# Revit family: Montageschiene 27- 18-1,25 fbv 2m Langloch 2D
name_source: partatom
category: HLS-Bauteile
units: mm (PartAtom-declared; Revit-internal decimal feet)

## family parameters
Arbeitsebenenbasiert = Ja
Beim Laden mit Abzugskörper schneiden = Nein
Bemaßung runder Anschluss = Durchmesser verwenden
Beschriftungsausrichtung beibehalten = Nein
Gemeinsam genutzt = Ja
Immer vertikal = Nein
Raumberechnungspunkt = Nein
Teiletyp = Normal

## types (1)
- Profil  27- 18-1,25 fbv L=2000
    Abmessung = 27/18/1.25 mm
    Artikelnummer = 1240013
    Breite = 27 mm  [stored 0.0885827 ft]
    Bund = 800 m
    EAN = 4250928424259
    Fabrikat = MEFA
    Firma = MEFA Befestigungs- und Montagesysteme GmbH
    Fläche (schwächster Profilquerschnitt) = 0 m²
    Gewicht = 0,60 kg
    Höhe = 18 mm
    Kurztext1 = Montageschiene C-Profil
    Kurztext2 = 27 / 18 / 1,25 mm L= 2 m fbv
    Langloch = 10.5 x 38.5 mm
    Länge = 2000 mm  [stored 6.56168 ft]
    Material = Stahl
    Materialname = S250
    Mengeneinheit = m
    Oberflaeche = feuerbandverzinkt
    Profil = C-Profil
    Profiltyp = 27/18
    Schlitzbreite = 14.0 mm
    Schwerpunktabstand eo = 0.85 cm
    Schwerpunktabstand eu = 0.95 cm
    Schwerpunktabstand ez = 1.35 cm
    Streckgrenze = 250 N/mm²
    Stärke = 1 mm  [stored 0.00328084 ft]
    Torsionswiderstandsmoment Wt = cm³
    Trägheitsradius iy = 0.65 cm
    Trägheitsradius iz = 1.15 cm
    Vorgabe-Ansicht = 1219 mm
    Widerstandsmoment Wy = 0.31 cm³
    Widerstandsmoment Wz = 0.67 cm³
    vpe = 20

note: [stored X ft] marks values corroborated as IEEE doubles in the binary element streams (Revit-internal decimal feet)
